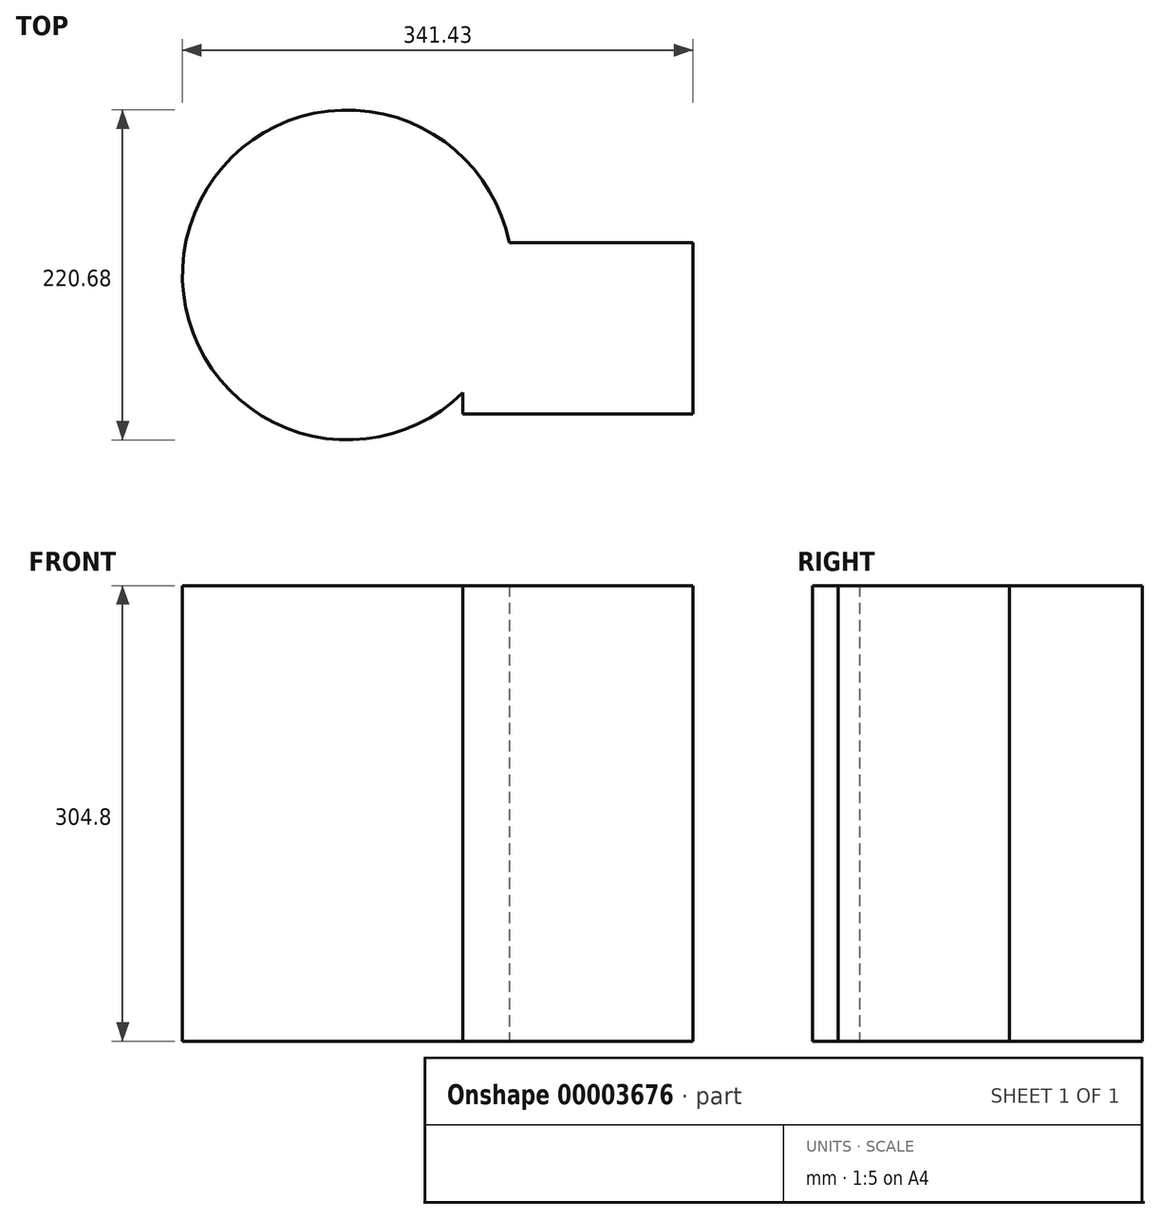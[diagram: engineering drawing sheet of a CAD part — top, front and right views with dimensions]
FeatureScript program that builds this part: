
annotation { "Feature Type Name" : "Feature", "Feature Type Description" : "" }
export const myFeature = defineFeature(function(context is Context, id is Id, definition is map)
    precondition{}
    {
        {
            var Q0;
            Q0=qCreatedBy(makeId("Top.planeOp"),FACE);
            var sketch = newSketch(context, id + "F0", { "sketchPlane" : qUnion([Q0])});
            skLineSegment(sketch, "E0.bottom", {"start": v(-3.8, 31.73) * mm, "end": v(119.09, 31.73) * mm});
            skLineSegment(sketch, "E0.top", {"start": v(-34.72, -82.87) * mm, "end": v(119.09, -82.87) * mm});
            skLineSegment(sketch, "E0.right", {"start": v(119.09, 31.73) * mm, "end": v(119.09, -82.87) * mm});
            skArc(sketch, "E1", {"start": v(-3.8, 31.73) * mm, "mid": v(-217.45, 42.55) * mm, "end": v(-34.72, -68.69) * mm});
            skLineSegment(sketch, "E2.trimOffspring", {"start": v(-34.72, -68.69) * mm, "end": v(-34.72, -82.87) * mm});
            skSolve(sketch);
        }
        {
            var Q0;
            Q0=makeQuery(id+"F0.imprint","IMPRINT",FACE,{"disambiguationData":[TD([[makeQuery(id+"F0.imprint","IMPRINT",EDGE,{"derivedFrom":sQuery(id+"F0.wireOp",EDGE,"E0.bottom")}),-1.0]])]});
            extrude(context, id + "F1", {"entities" : qUnion([Q0]), "depth" : 304.8 * mm, "offsetDistance" : 25.4 * mm});
        }
    });
